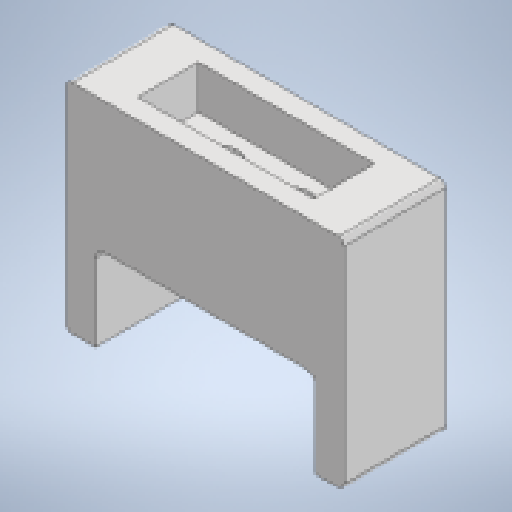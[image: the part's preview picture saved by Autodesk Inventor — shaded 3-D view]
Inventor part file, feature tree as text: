
AUTODESK INVENTOR PART (.ipt)
format: ipt  version: 2023 (Build 270158000, 158)  size: 202,752 bytes
history: native  units: in
note: dims shown in document units (in); Inventor stores cm internally (conversion verified against a paired STEP export)
features: extrude x7, sketch x6, fillet x2
ambient origin geometry x8: Origin, YZ Plane, XZ Plane, XY Plane, X Axis, Y Axis, Z Axis, Center Point
bodies: Solid1 (feature_tree)
feature tree (15):
  sketch  "Sketch1"  dims[d0=0.7874in d1=2.3622in]
  extrude  "Extrusion1"  Depth=2.3622in
  extrude  "Extrusion2"  Depth=0.0197in
  extrude  "Extrusion3"  Depth=0.0197in
  extrude  "Extrusion4"  Depth=1.811in
  extrude  "Extrusion5"  Depth=1.378in
  extrude  "Extrusion6"  Depth=1.378in TaperAngle=0.0deg
  fillet  "Fillet1"  Radius=0.3937in
  fillet  "Fillet2"  Radius=0.3937in
  extrude  "Extrusion7"  Depth=3.0in
  sketch  "Sketch2"  dims[d2=0.0197in d3=0.0197in]
  sketch  "Sketch3"  dims[d4=0.0197in d5=0.0197in]
  sketch  "Sketch4"  dims[d6=0.1417in d7=1.811in]
  sketch  "Sketch5"  dims[d9=3.7874in d10=1.378in]
  sketch  "Sketch6"  dims[d11=0.3937in d12=0.0in d13=1.3937in d14=0.0in d15=0.3937in d16=0.1969in d17=0.0in d18=0.0in d19=0.3937in d20=1.1969in d21=0.0in d22=0.0in d23=3.0in d24=0.125in d25=0.3937in d26=1.1811in d27=0.3937in d28=0.0in d29=0.2362in d30=0.9843in d31=0.3937in d32=0.0in d34=0.4724in d35=0.3937in d36=0.0in d37=0.0787in d38=0.0787in d39=1.5118in d40=1.378in d41=2.0812in d42=0.0in]
